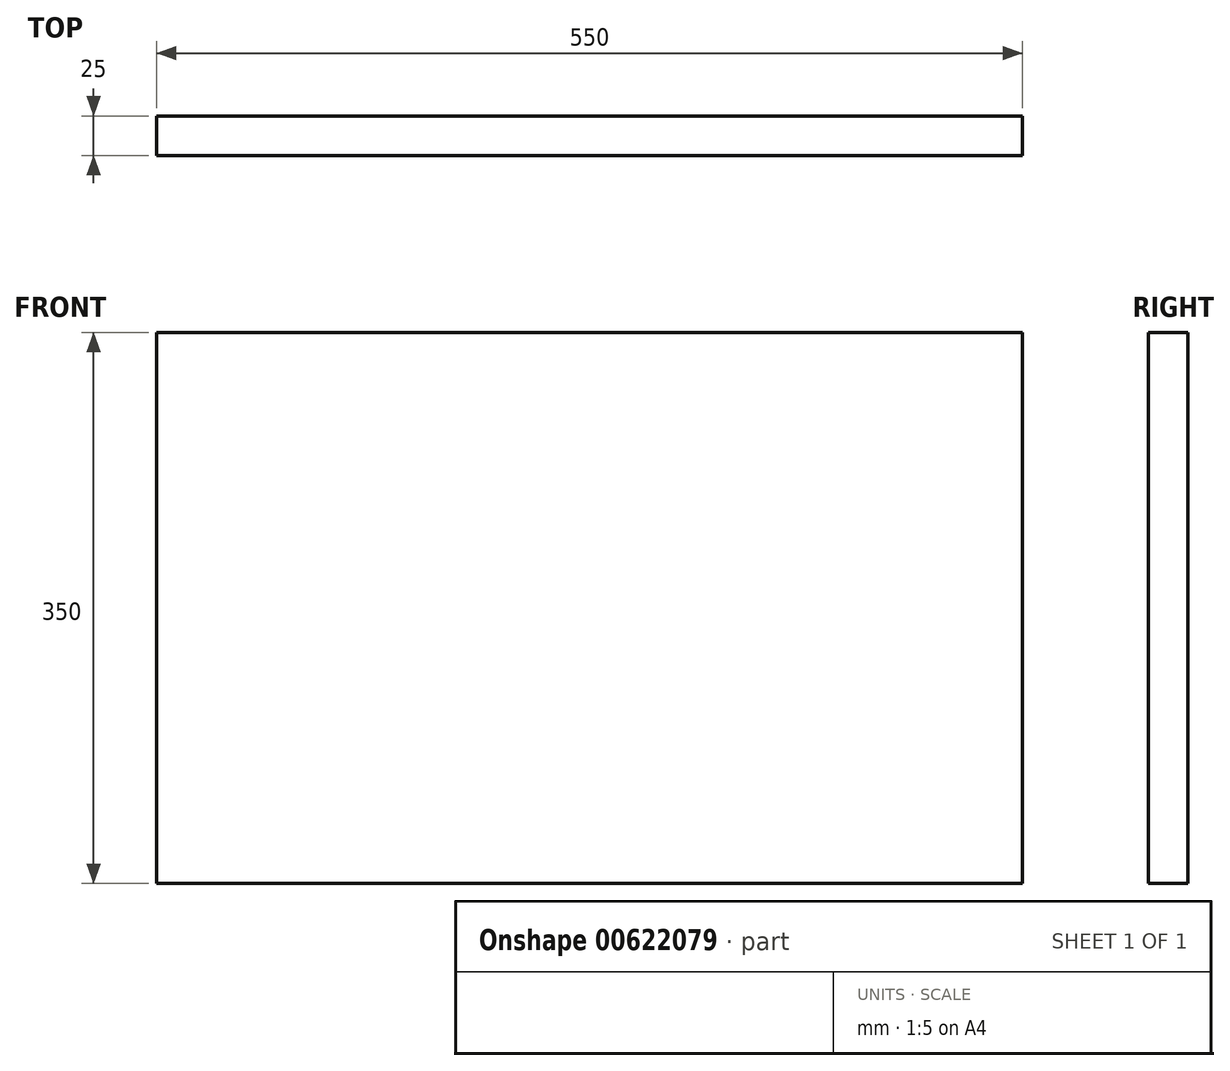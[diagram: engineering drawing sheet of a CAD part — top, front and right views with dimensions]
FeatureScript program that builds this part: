
annotation { "Feature Type Name" : "Feature", "Feature Type Description" : "" }
export const myFeature = defineFeature(function(context is Context, id is Id, definition is map)
    precondition{}
    {
        {
            var Q0;
            Q0=qCreatedBy(makeId("Front.planeOp"),FACE);
            var sketch = newSketch(context, id + "F0", { "sketchPlane" : qUnion([Q0])});
            skLineSegment(sketch, "E0.bottom", {"start": v(-275, 175) * mm, "end": v(275, 175) * mm});
            skLineSegment(sketch, "E0.top", {"start": v(-275, -175) * mm, "end": v(275, -175) * mm});
            skLineSegment(sketch, "E0.left", {"start": v(-275, 175) * mm, "end": v(-275, -175) * mm});
            skLineSegment(sketch, "E0.right", {"start": v(275, 175) * mm, "end": v(275, -175) * mm});
            skPoint(sketch, "E0.middle", {"position": v(0, 0) * mm});
            skSolve(sketch);
        }
        {
            var Q0;
            Q0=makeQuery(id+"F0.imprint","IMPRINT",FACE,{"disambiguationData":[TD([[makeQuery(id+"F0.imprint","IMPRINT",EDGE,{"derivedFrom":sQuery(id+"F0.wireOp",EDGE,"E0.bottom")}),-1.0]])]});
            extrude(context, id + "F1", {"entities" : qUnion([Q0]), "depth" : 25 * mm, "offsetDistance" : 25 * mm});
        }
    });
